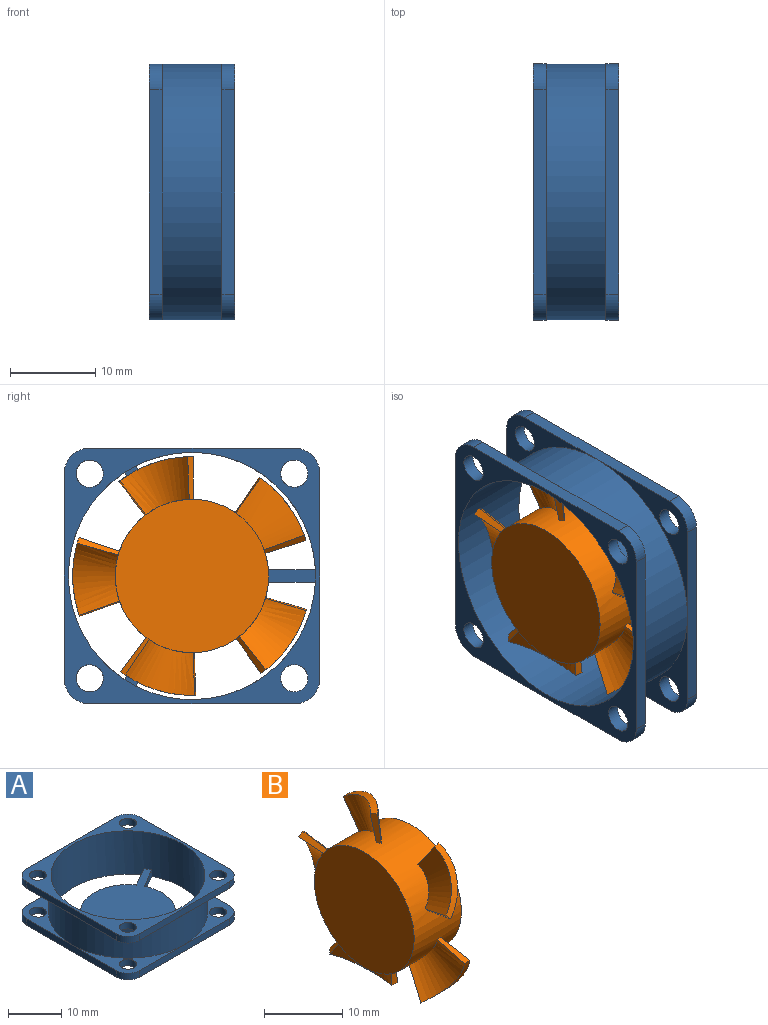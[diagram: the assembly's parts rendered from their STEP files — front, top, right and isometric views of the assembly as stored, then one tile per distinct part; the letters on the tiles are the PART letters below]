
ASSEMBLY  parts=2 mates=1
PART A: 46 faces, bbox 30x30x10 mm
  f0: cylinder r=9mm len=12.8mm, axis (0,0,-1), area 26mm2, adj f11,f37,f39,f41
  f1: cylinder r=1.6mm len=3.2mm, axis (0,0,-1), area 15.1mm2, adj f11,f13
  f2: cylinder r=1.6mm len=3.2mm, axis (0,0,-1), area 15.1mm2, adj f12,f14
  f3: cylinder r=1.6mm len=3.2mm, axis (0,0,-1), area 15.1mm2, adj f11,f15
  f4: cylinder r=1.6mm len=3.2mm, axis (0,0,-1), area 15.1mm2, adj f12,f16
  f5: cylinder r=1.6mm len=3.2mm, axis (0,0,-1), area 15.1mm2, adj f11,f17
  f6: cylinder r=1.6mm len=3.2mm, axis (0,0,-1), area 15.1mm2, adj f12,f18
  f7: cylinder r=1.6mm len=3.2mm, axis (0,0,-1), area 15.1mm2, adj f11,f19
  f8: cylinder r=1.6mm len=3.2mm, axis (0,0,-1), area 15.1mm2, adj f12,f20
  f9: cylinder r=15mm len=30mm, axis (0,0,1), area 659.7mm2, adj f13,f14,f15,f16,f17,f18,f19,f20
  f10: cylinder r=14.5mm len=29mm, axis (0,0,-1), area 904.3mm2, adj f11,f12,f37,f38,f39,f40,f41,f42
  f11: plane 30x30mm, normal (0,0,-1), area 478.8mm2, adj f0,f1,f3,f5,f7,f10,f21,f23
  f12: plane 30x30mm, normal (0,0,1), area 199.6mm2, adj f2,f4,f6,f8,f10,f22,f24,f26
  f13: plane 15x15mm, normal (0,0,1), area 38.3mm2, adj f1,f9,f25,f27,f29
  f14: plane 15x15mm, normal (0,0,-1), area 38.3mm2, adj f2,f9,f26,f28,f30
  f15: plane 15x15mm, normal (0,0,1), area 38.3mm2, adj f3,f9,f21,f23,f25
  f16: plane 15x15mm, normal (0,0,-1), area 38.3mm2, adj f4,f9,f22,f24,f26
  f17: plane 15x15mm, normal (0,0,1), area 38.3mm2, adj f5,f9,f21,f33,f35
  f18: plane 15x15mm, normal (0,0,-1), area 38.3mm2, adj f6,f9,f22,f34,f36
  f19: plane 15x15mm, normal (0,0,1), area 38.3mm2, adj f7,f9,f29,f31,f33
  f20: plane 15x15mm, normal (0,0,-1), area 38.3mm2, adj f8,f9,f30,f32,f34
  f21: plane 24x1.5mm, normal (0,-1,0), area 36mm2, adj f11,f15,f17,f23,f35
  f22: plane 24x1.5mm, normal (0,-1,0), area 36mm2, adj f12,f16,f18,f24,f36
  f23: cylinder r=3mm len=3mm, axis (0,0,-1), area 7.1mm2, adj f11,f15,f21,f25
  f24: cylinder r=3mm len=3mm, axis (0,0,-1), area 7.1mm2, adj f12,f16,f22,f26
  f25: plane 24x1.5mm, normal (-1,0,0), area 36mm2, adj f11,f13,f15,f23,f27
  f26: plane 24x1.5mm, normal (-1,0,0), area 36mm2, adj f12,f14,f16,f24,f28
  f27: cylinder r=3mm len=3mm, axis (0,0,-1), area 7.1mm2, adj f11,f13,f25,f29
  f28: cylinder r=3mm len=3mm, axis (0,0,-1), area 7.1mm2, adj f12,f14,f26,f30
  f29: plane 24x1.5mm, normal (0,1,0), area 36mm2, adj f11,f13,f19,f27,f31
  f30: plane 24x1.5mm, normal (0,1,0), area 36mm2, adj f12,f14,f20,f28,f32
  f31: cylinder r=3mm len=3mm, axis (0,0,-1), area 7.1mm2, adj f11,f19,f29,f33
  f32: cylinder r=3mm len=3mm, axis (0,0,-1), area 7.1mm2, adj f12,f20,f30,f34
  f33: plane 24x1.5mm, normal (1,0,0), area 36mm2, adj f11,f17,f19,f31,f35
  f34: plane 24x1.5mm, normal (1,0,0), area 36mm2, adj f12,f18,f20,f32,f36
  f35: cylinder r=3mm len=3mm, axis (0,0,-1), area 7.1mm2, adj f11,f17,f21,f33
  f36: cylinder r=3mm len=3mm, axis (0,0,-1), area 7.1mm2, adj f12,f18,f22,f34
  f37: plane 5.51x1.5mm, normal (-1,0,0), area 8.3mm2, adj f0,f10,f11,f39
  f38: plane 5.51x1.5mm, normal (1,0,0), area 8.3mm2, adj f10,f11,f39,f44
  f39: plane 25.83x23.5mm, normal (0,0,1), area 279.2mm2, adj f0,f10,f37,f38,f40,f41,f42,f43
  f40: plane 4.77x2.76mm, normal (0.5,0.87,0), area 8.3mm2, adj f10,f11,f39,f45
  f41: plane 4.77x2.76mm, normal (-0.5,-0.87,0), area 8.3mm2, adj f0,f10,f11,f39
  f42: plane 4.77x2.76mm, normal (0.5,-0.87,0), area 8.3mm2, adj f10,f11,f39,f44
  f43: plane 4.77x2.76mm, normal (-0.5,0.87,0), area 8.3mm2, adj f10,f11,f39,f45
  f44: cylinder r=9mm len=12.8mm, axis (0,0,-1), area 26mm2, adj f11,f38,f39,f42
  f45: cylinder r=9mm len=14.78mm, axis (0,0,-1), area 26mm2, adj f11,f39,f40,f43
PART B: 28 faces, bbox 8.5x28.2x29.6 mm
  f0: cylinder r=14mm len=8.81mm, axis (1,0,0), area 9.9mm2, adj f18,f19,f20,f21
  f1: cylinder r=9mm len=18mm, axis (-1,0,0), area 460.6mm2, adj f2,f3,f4,f5,f6,f7,f8,f9
  f2: bspline ~8.51x4.96mm, area 35.5mm2, adj f1,f3,f4,f27
  f3: plane 4.76x1.78mm, normal (-0.16,-0.32,-0.93), area 3.9mm2, adj f1,f2,f5,f27
  f4: plane 4.94x2.04mm, normal (-0.73,-0.32,0.61), area 3.9mm2, adj f1,f2,f5,f27
  f5: bspline ~9.27x4.79mm, area 38.4mm2, adj f1,f3,f4,f27
  f6: bspline ~8.28x6.82mm, area 36.8mm2, adj f1,f7,f8,f26
  f7: plane 4.05x3.14mm, normal (-0.16,0.79,-0.59), area 3.9mm2, adj f1,f6,f9,f26
  f8: plane 5.01x1.38mm, normal (-0.73,-0.68,-0.11), area 3.9mm2, adj f1,f6,f9,f26
  f9: bspline ~9.32x8.19mm, area 40.1mm2, adj f1,f7,f8,f26
  f10: bspline ~8.66x8mm, area 36.8mm2, adj f1,f11,f12,f25
  f11: plane 4.19x2.94mm, normal (-0.16,0.81,0.57), area 3.9mm2, adj f1,f10,f13,f25
  f12: plane 4.92x2.14mm, normal (-0.73,-0.1,-0.68), area 3.9mm2, adj f1,f10,f13,f25
  f13: bspline ~9.85x9.43mm, area 40.1mm2, adj f1,f11,f12,f25
  f14: bspline ~9.11x9.03mm, area 36.8mm2, adj f1,f15,f16,f24
  f15: plane 4.83x1.55mm, normal (-0.16,-0.29,0.94), area 3.9mm2, adj f1,f14,f17,f24
  f16: plane 4.35x3.44mm, normal (-0.73,0.62,-0.31), area 3.9mm2, adj f1,f14,f17,f24
  f17: bspline ~8.92x8.36mm, area 40.1mm2, adj f1,f15,f16,f24
  f18: bspline ~8.42x7.99mm, area 36.8mm2, adj f0,f1,f19,f20
  f19: plane 5x1.07mm, normal (-0.16,-0.99,0.01), area 3.9mm2, adj f0,f1,f18,f21
  f20: plane 4.41x3.36mm, normal (-0.73,0.48,0.49), area 3.9mm2, adj f0,f1,f18,f21
  f21: bspline ~8.82x6.91mm, area 40.1mm2, adj f0,f1,f19,f20
  f22: plane 18x18mm, normal (1,0,0), area 254.5mm2, adj f1
  f23: plane 18x18mm, normal (-1,0,0), area 254.5mm2, adj f1
  f24: cylinder r=14mm len=7.52mm, axis (1,0,0), area 9.8mm2, adj f14,f15,f16,f17
  f25: cylinder r=14mm len=7.43mm, axis (1,0,0), area 9.8mm2, adj f10,f11,f12,f13
  f26: cylinder r=14mm len=8.76mm, axis (1,0,0), area 9.8mm2, adj f6,f7,f8,f9
  f27: cylinder r=14mm len=9.24mm, axis (1,0,0), area 9.8mm2, adj f2,f3,f4,f5
PLACE A rot(axis=(0,-1,0),90deg) t=(-15,0,15)mm
PLACE B t=(-15,0,15)mm
MATE fastened B.f1 <-> A.f0  axis (1,0,0) through (-16.5,0,15)mm
